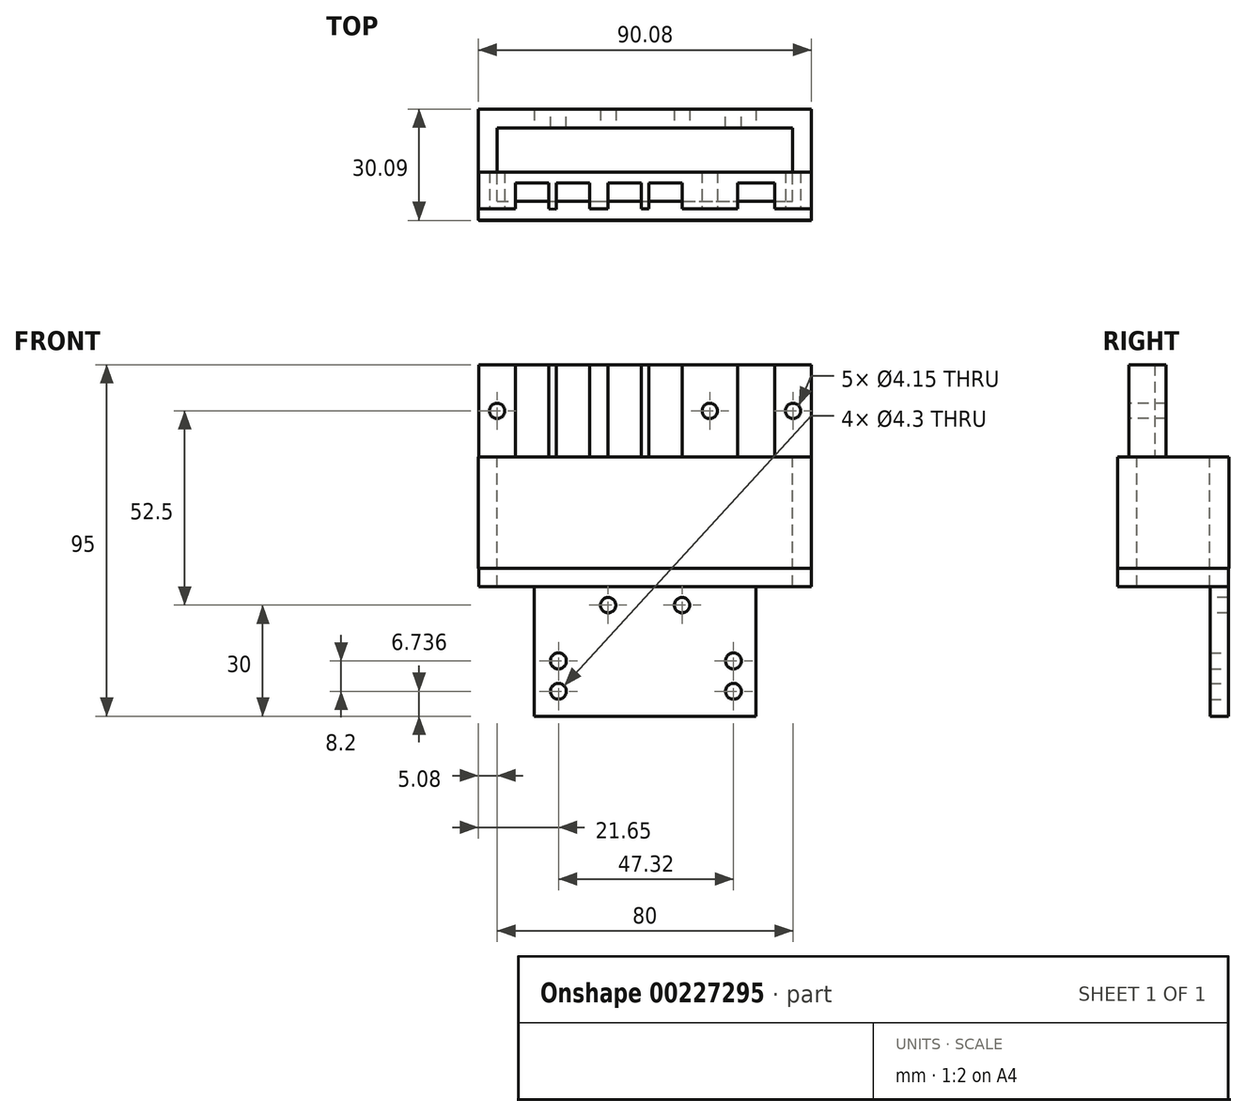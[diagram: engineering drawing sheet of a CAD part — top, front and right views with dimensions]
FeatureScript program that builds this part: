
annotation { "Feature Type Name" : "Feature", "Feature Type Description" : "" }
export const myFeature = defineFeature(function(context is Context, id is Id, definition is map)
    precondition{}
    {
        {
            var Q0;
            Q0=qCreatedBy(makeId("Top.planeOp"),FACE);
            var sketch = newSketch(context, id + "F0", { "sketchPlane" : qUnion([Q0])});
            skLineSegment(sketch, "E0", {"start": v(-45, 0) * mm, "end": v(45, 0) * mm});
            skLineSegment(sketch, "E1", {"start": v(-45, 0) * mm, "end": v(-45, -10) * mm});
            skLineSegment(sketch, "E2", {"start": v(-45, -10) * mm, "end": v(-35, -10) * mm});
            skLineSegment(sketch, "E3", {"start": v(-35, -3) * mm, "end": v(-26, -3) * mm});
            skLineSegment(sketch, "E4", {"start": v(-24, -10) * mm, "end": v(-24, -3) * mm});
            skLineSegment(sketch, "E5", {"start": v(-24, -3) * mm, "end": v(-15, -3) * mm});
            skLineSegment(sketch, "E6", {"start": v(-10, -3) * mm, "end": v(-1, -3) * mm});
            skLineSegment(sketch, "E7", {"start": v(1, -3) * mm, "end": v(10, -3) * mm});
            skLineSegment(sketch, "E8", {"start": v(25, -3) * mm, "end": v(35, -3) * mm});
            skLineSegment(sketch, "E9", {"start": v(35, -10) * mm, "end": v(45, -10) * mm});
            skLineSegment(sketch, "E10", {"start": v(45, -10) * mm, "end": v(45, 0) * mm});
            skLineSegment(sketch, "E11.bottom", {"start": v(-20, 0) * mm, "end": v(20, 0) * mm});
            skLineSegment(sketch, "E11.left", {"start": v(-20, 0) * mm, "end": v(-20, 0) * mm});
            skLineSegment(sketch, "E11.right", {"start": v(20, 0) * mm, "end": v(20, 0) * mm});
            skLineSegment(sketch, "E12", {"start": v(-26, -3) * mm, "end": v(-26, -10) * mm});
            skLineSegment(sketch, "E13", {"start": v(-26, -10) * mm, "end": v(-24, -10) * mm});
            skLineSegment(sketch, "E14", {"start": v(-15, -3) * mm, "end": v(-15, -10) * mm});
            skLineSegment(sketch, "E15", {"start": v(-15, -10) * mm, "end": v(-10, -10) * mm});
            skLineSegment(sketch, "E16", {"start": v(-10, -10) * mm, "end": v(-10, -3) * mm});
            skPoint(sketch, "E17.start.orphan", {"position": v(-1, -10) * mm});
            skLineSegment(sketch, "E18", {"start": v(-1, -3) * mm, "end": v(-1, -10) * mm});
            skLineSegment(sketch, "E19", {"start": v(-1, -10) * mm, "end": v(1, -10) * mm});
            skLineSegment(sketch, "E20", {"start": v(1, -10) * mm, "end": v(1, -3) * mm});
            skPoint(sketch, "E21.start.orphan", {"position": v(10, -10) * mm});
            skLineSegment(sketch, "E22", {"start": v(10, -3) * mm, "end": v(10, -10) * mm});
            skLineSegment(sketch, "E23", {"start": v(10, -10) * mm, "end": v(25, -10) * mm});
            skLineSegment(sketch, "E24", {"start": v(25, -10) * mm, "end": v(25, -3) * mm});
            skLineSegment(sketch, "E25", {"start": v(-35, -3) * mm, "end": v(-35, -10) * mm});
            skLineSegment(sketch, "E26", {"start": v(35, -3) * mm, "end": v(35, -10) * mm});
            skPoint(sketch, "E27.start.orphan", {"position": v(35, -12) * mm});
            skPoint(sketch, "E28.start.orphan", {"position": v(-35, -12) * mm});
            skSolve(sketch);
        }
        {
            var Q0;
            {var subQ2=sQuery(id+"F0.wireOp",EDGE,"E1");Q0=makeQuery(id+"F0.imprint","IMPRINT",FACE,{"disambiguationData":[TD([[makeQuery(id+"F0.imprint","IMPRINT",EDGE,{"derivedFrom":subQ2}),1.0]])]});}
            extrude(context, id + "F1", {"entities" : qUnion([Q0]), "depth" : 25 * mm});
        }
        {
            var Q0;
            Q0=qCreatedBy(makeId("Top.planeOp"),FACE);
            var sketch = newSketch(context, id + "F2", { "sketchPlane" : qUnion([Q0])});
            skLineSegment(sketch, "E29.bottom", {"start": v(-45.08, -12.97) * mm, "end": v(44.92, -12.97) * mm});
            skLineSegment(sketch, "E29.top", {"start": v(-45.08, 17.03) * mm, "end": v(44.92, 17.03) * mm});
            skLineSegment(sketch, "E29.left", {"start": v(-45.08, -12.97) * mm, "end": v(-45.08, 17.03) * mm});
            skLineSegment(sketch, "E29.right", {"start": v(44.92, -12.97) * mm, "end": v(44.92, 17.03) * mm});
            skLineSegment(sketch, "E30.0", {"start": v(-39.98, -7.87) * mm, "end": v(39.82, -7.87) * mm});
            skLineSegment(sketch, "E30.1", {"start": v(-39.98, -7.87) * mm, "end": v(-39.98, 11.93) * mm});
            skLineSegment(sketch, "E30.2", {"start": v(-39.98, 11.93) * mm, "end": v(39.82, 11.93) * mm});
            skLineSegment(sketch, "E30.3", {"start": v(39.82, -7.87) * mm, "end": v(39.82, 11.93) * mm});
            skSolve(sketch);
        }
        {
            var Q0;
            Q0 = qSketchRegion(id + "F2", true);
            extrude(context, id + "F3", {"entities" : qUnion([Q0]), "operationType" : NewBodyOperationType.ADD, "oppositeDirection" : true, "depth" : 30 * mm});
        }
        {
            var Q0;
            Q0=makeQuery(id+"F3.opExtrude","CAP_FACE",FACE,{"disambiguationData":[OSD([sQuery(id+"F2.wireOp",EDGE,"E29.bottom"),sQuery(id+"F2.wireOp",EDGE,"E29.top"),sQuery(id+"F2.wireOp",EDGE,"E29.left"),sQuery(id+"F2.wireOp",EDGE,"E29.right"),sQuery(id+"F2.wireOp",EDGE,"E30.0"),sQuery(id+"F2.wireOp",EDGE,"E30.1"),sQuery(id+"F2.wireOp",EDGE,"E30.2"),sQuery(id+"F2.wireOp",EDGE,"E30.3")])],"isStart":false});
            cPlane(context, id + "F4", {"entities" : qUnion([Q0]), "cplaneType" : CPlaneType.OFFSET, "offset" : 0 * mm, "width" : 150 * mm, "height" : 150 * mm});
        }
        {
            var Q0;
            Q0=qCreatedBy(id+"F4.planeOp",FACE);
            var sketch = newSketch(context, id + "F5", { "sketchPlane" : qUnion([Q0])});
            skLineSegment(sketch, "E31.bottom", {"start": v(-45, 13.06) * mm, "end": v(45, 13.06) * mm});
            skLineSegment(sketch, "E31.top", {"start": v(-45, -16.94) * mm, "end": v(45, -16.94) * mm});
            skLineSegment(sketch, "E31.left", {"start": v(-45, 13.06) * mm, "end": v(-45, -16.94) * mm});
            skLineSegment(sketch, "E31.right", {"start": v(45, 13.06) * mm, "end": v(45, -16.94) * mm});
            skSolve(sketch);
        }
        {
            var Q0;
            Q0=makeQuery(id+"F5.imprint","IMPRINT",FACE,{"disambiguationData":[TD([[makeQuery(id+"F5.imprint","IMPRINT",EDGE,{"derivedFrom":sQuery(id+"F5.wireOp",EDGE,"E31.bottom")}),-1.0]])]});
            extrude(context, id + "F6", {"entities" : qUnion([Q0]), "operationType" : NewBodyOperationType.ADD, "depth" : 5 * mm});
        }
        {
            var Q0;
            Q0=makeQuery(id+"F6.opExtrude","CAP_FACE",FACE,{"disambiguationData":[OSD([sQuery(id+"F5.wireOp",EDGE,"E31.bottom"),sQuery(id+"F5.wireOp",EDGE,"E31.top"),sQuery(id+"F5.wireOp",EDGE,"E31.left"),sQuery(id+"F5.wireOp",EDGE,"E31.right")])],"isStart":false});
            var sketch = newSketch(context, id + "F7", { "sketchPlane" : qUnion([Q0])});
            skLineSegment(sketch, "E32.bottom", {"start": v(-30, -16.94) * mm, "end": v(30, -16.94) * mm});
            skLineSegment(sketch, "E32.top", {"start": v(-30, -11.94) * mm, "end": v(30, -11.94) * mm});
            skLineSegment(sketch, "E32.left", {"start": v(-30, -16.94) * mm, "end": v(-30, -11.94) * mm});
            skLineSegment(sketch, "E32.right", {"start": v(30, -16.94) * mm, "end": v(30, -11.94) * mm});
            skLineSegment(sketch, "E33", {"start": v(0, -16.94) * mm, "end": v(0, -9.1) * mm, "construction": true});
            skSolve(sketch);
        }
        {
            var Q0;
            Q0=makeQuery(id+"F7.imprint","IMPRINT",FACE,{"disambiguationData":[TD([[makeQuery(id+"F7.imprint","IMPRINT",EDGE,{"derivedFrom":sQuery(id+"F7.wireOp",EDGE,"E32.bottom")}),1.0]])]});
            extrude(context, id + "F8", {"entities" : qUnion([Q0]), "operationType" : NewBodyOperationType.ADD, "depth" : 35 * mm});
        }
        {
            var Q0;
            Q0=makeQuery(id+"F8.opExtrude","SWEPT_FACE",FACE,{"disambiguationData":[OSD([sQuery(id+"F7.wireOp",EDGE,"E32.top")])]});
            var sketch = newSketch(context, id + "F9", { "sketchPlane" : qUnion([Q0])});
            skCircle(sketch, "E34", {"center": v(-10, -40) * mm, "radius": 2.08 * mm});
            skCircle(sketch, "E35", {"center": v(10, -40) * mm, "radius": 2.08 * mm});
            skSolve(sketch);
        }
        {
            var Q0;
            Q0=makeQuery(id+"F9.imprint","IMPRINT",FACE,{"disambiguationData":[TD([[makeQuery(id+"F9.imprint","IMPRINT",EDGE,{"derivedFrom":sQuery(id+"F9.wireOp",EDGE,"E34")}),1.0]])]});
            var Q1;
            Q1=makeQuery(id+"F9.imprint","IMPRINT",FACE,{"disambiguationData":[TD([[makeQuery(id+"F9.imprint","IMPRINT",EDGE,{"derivedFrom":sQuery(id+"F9.wireOp",EDGE,"E35")}),1.0]])]});
            var Q2;
            Q2=sQuery(id+"F9.wireOp",EDGE,"E34");
            var Q3;
            Q3=sQuery(id+"F9.wireOp",EDGE,"E35");
            extrude(context, id + "F10", {"entities" : qUnion([Q0, Q1]), "operationType" : NewBodyOperationType.REMOVE, "surfaceEntities" : qUnion([Q2, Q3]), "endBound" : BoundingType.UP_TO_NEXT, "oppositeDirection" : true, "depth" : 25 * mm});
        }
        {
            var Q0;
            Q0=makeQuery(id+"F1.opExtrude","SWEPT_FACE",FACE,{"disambiguationData":[OSD([sQuery(id+"F0.wireOp",EDGE,"E0"),sQuery(id+"F0.wireOp",EDGE,"E11.bottom")])]});
            cPlane(context, id + "F11", {"entities" : qUnion([Q0]), "cplaneType" : CPlaneType.OFFSET, "offset" : 10 * mm, "oppositeDirection" : true, "width" : 150 * mm, "height" : 150 * mm});
        }
        {
            var Q0;
            Q0=qCreatedBy(id+"F11.planeOp",FACE);
            var sketch = newSketch(context, id + "F12", { "sketchPlane" : qUnion([Q0])});
            skCircle(sketch, "E36", {"center": v(40, 12.5) * mm, "radius": 2.08 * mm});
            skCircle(sketch, "E37", {"center": v(-17.5, 12.5) * mm, "radius": 2.08 * mm});
            skCircle(sketch, "E38", {"center": v(-40, 12.5) * mm, "radius": 2.08 * mm});
            skSolve(sketch);
        }
        {
            var Q0;
            Q0=makeQuery(id+"F12.imprint","IMPRINT",FACE,{"disambiguationData":[TD([[makeQuery(id+"F12.imprint","IMPRINT",EDGE,{"derivedFrom":sQuery(id+"F12.wireOp",EDGE,"E36")}),1.0]])]});
            var Q1;
            Q1=makeQuery(id+"F12.imprint","IMPRINT",FACE,{"disambiguationData":[TD([[makeQuery(id+"F12.imprint","IMPRINT",EDGE,{"derivedFrom":sQuery(id+"F12.wireOp",EDGE,"E37")}),1.0]])]});
            var Q2;
            Q2=makeQuery(id+"F12.imprint","IMPRINT",FACE,{"disambiguationData":[TD([[makeQuery(id+"F12.imprint","IMPRINT",EDGE,{"derivedFrom":sQuery(id+"F12.wireOp",EDGE,"E38")}),1.0]])]});
            extrude(context, id + "F13", {"entities" : qUnion([Q0, Q1, Q2]), "operationType" : NewBodyOperationType.REMOVE, "endBound" : BoundingType.UP_TO_NEXT, "depth" : 25 * mm});
        }
        {
            var Q0;
            Q0=makeQuery(id+"F8.boolean.opBoolean","MERGE",FACE,{"derivedFrom":[makeQuery(id+"F6.opExtrude","SWEPT_FACE",FACE,{"disambiguationData":[OSD([sQuery(id+"F5.wireOp",EDGE,"E31.top")])]}),makeQuery(id+"F8.opExtrude","SWEPT_FACE",FACE,{"disambiguationData":[OSD([sQuery(id+"F7.wireOp",EDGE,"E32.bottom")])]})]});
            cPlane(context, id + "F14", {"entities" : qUnion([Q0]), "cplaneType" : CPlaneType.OFFSET, "offset" : 0 * mm, "width" : 150 * mm, "height" : 150 * mm});
        }
        {
            var Q0;
            Q0=qCreatedBy(id+"F14.planeOp",FACE);
            var sketch = newSketch(context, id + "F15", { "sketchPlane" : qUnion([Q0])});
            skLineSegment(sketch, "E39.bottom", {"start": v(27.56, -46.9) * mm, "end": v(-27.94, -46.9) * mm, "construction": true});
            skLineSegment(sketch, "E39.top", {"start": v(27.56, -69.9) * mm, "end": v(-27.94, -69.9) * mm, "construction": true});
            skLineSegment(sketch, "E39.left", {"start": v(27.56, -46.9) * mm, "end": v(27.56, -69.9) * mm, "construction": true});
            skLineSegment(sketch, "E39.right", {"start": v(-27.94, -46.9) * mm, "end": v(-27.94, -69.9) * mm, "construction": true});
            skCircle(sketch, "E40", {"center": v(23.43, -55.06) * mm, "radius": 2.15 * mm});
            skCircle(sketch, "E41", {"center": v(-23.89, -55.06) * mm, "radius": 2.15 * mm});
            skCircle(sketch, "E42", {"center": v(-23.89, -63.26) * mm, "radius": 2.15 * mm});
            skCircle(sketch, "E43", {"center": v(23.43, -63.26) * mm, "radius": 2.15 * mm});
            skSolve(sketch);
        }
        {
            var Q0;
            Q0 = qSketchRegion(id + "F15", true);
            extrude(context, id + "F16", {"entities" : qUnion([Q0]), "operationType" : NewBodyOperationType.REMOVE, "endBound" : BoundingType.UP_TO_NEXT, "oppositeDirection" : true, "depth" : 25 * mm});
        }
        {
            var Q0;
            Q0=makeQuery(id+"F2.imprint","IMPRINT",FACE,{"disambiguationData":[TD([[makeQuery(id+"F2.imprint","IMPRINT",EDGE,{"derivedFrom":sQuery(id+"F2.wireOp",EDGE,"E30.0")}),1.0]])]});
            extrude(context, id + "F17", {"entities" : qUnion([Q0]), "operationType" : NewBodyOperationType.REMOVE, "oppositeDirection" : true, "depth" : 35 * mm});
        }
    });
